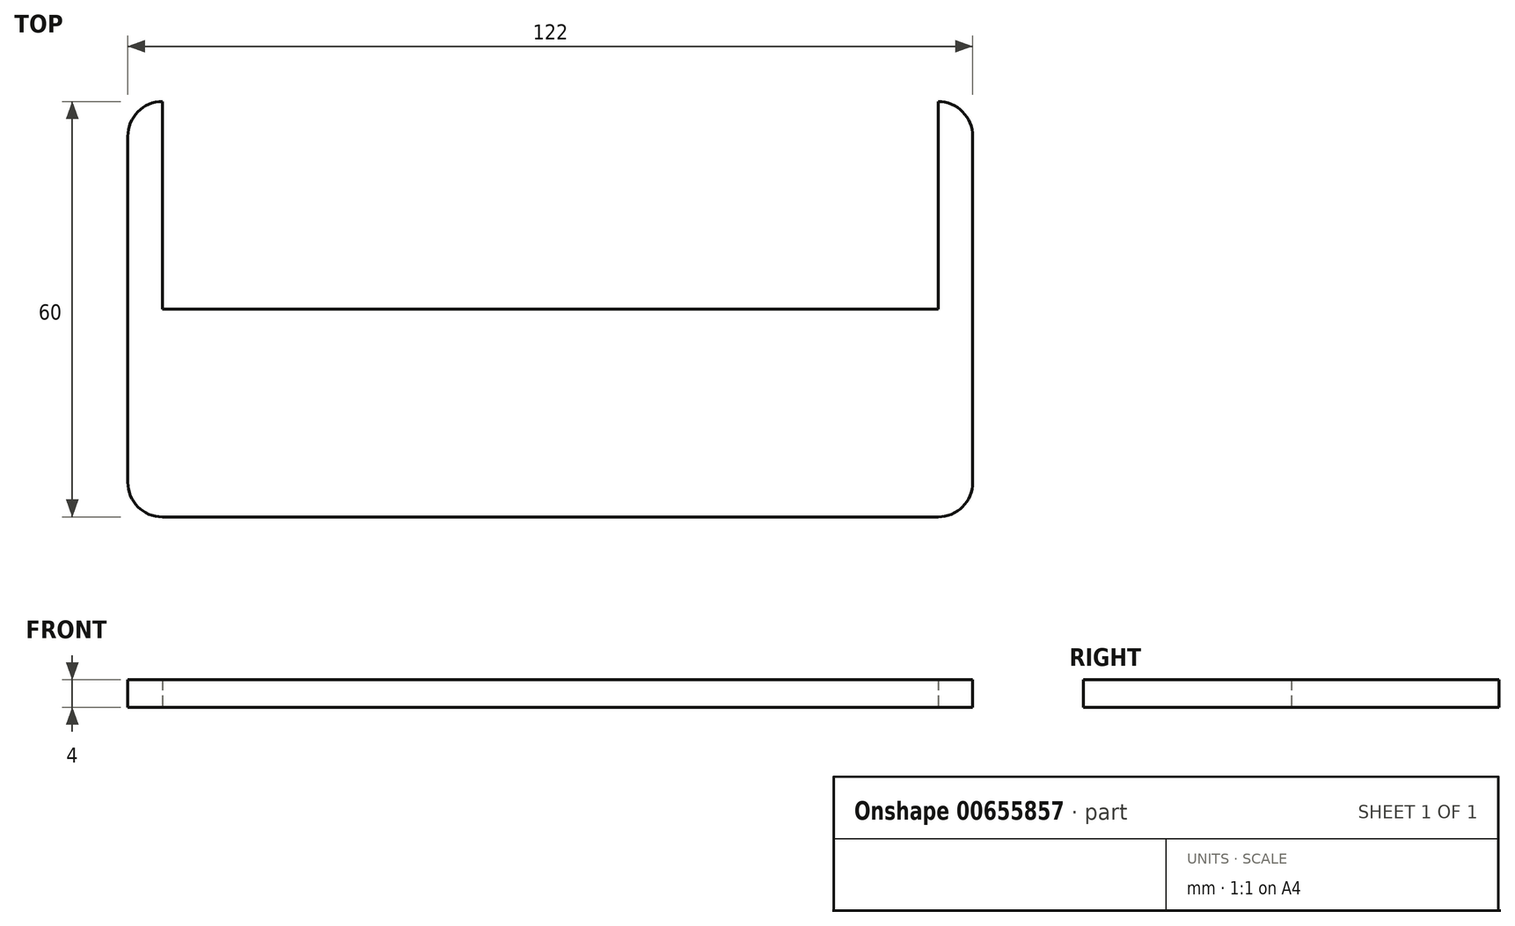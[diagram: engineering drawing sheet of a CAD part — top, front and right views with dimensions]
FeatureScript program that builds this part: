
annotation { "Feature Type Name" : "Feature", "Feature Type Description" : "" }
export const myFeature = defineFeature(function(context is Context, id is Id, definition is map)
    precondition{}
    {
        {
            var Q0;
            Q0=qCreatedBy(makeId("Top.planeOp"),FACE);
            var sketch = newSketch(context, id + "F0", { "sketchPlane" : qUnion([Q0])});
            skLineSegment(sketch, "E0.bottom", {"start": v(-56, 0) * mm, "end": v(56, 0) * mm});
            skLineSegment(sketch, "E0.top", {"start": v(-56, -30) * mm, "end": v(56, -30) * mm});
            skLineSegment(sketch, "E0.left", {"start": v(-56, 0) * mm, "end": v(-56, -30) * mm});
            skLineSegment(sketch, "E0.right", {"start": v(56, 0) * mm, "end": v(56, -30) * mm});
            skLineSegment(sketch, "E1.bottom", {"start": v(-56, -30) * mm, "end": v(-61, -30) * mm});
            skLineSegment(sketch, "E1.top", {"start": v(-56, 30) * mm, "end": v(-61, 30) * mm});
            skLineSegment(sketch, "E1.left", {"start": v(-56, -30) * mm, "end": v(-56, 30) * mm});
            skLineSegment(sketch, "E1.right", {"start": v(-61, -30) * mm, "end": v(-61, 30) * mm});
            skLineSegment(sketch, "E2.bottom", {"start": v(56, -30) * mm, "end": v(61, -30) * mm});
            skLineSegment(sketch, "E2.top", {"start": v(56, 30) * mm, "end": v(61, 30) * mm});
            skLineSegment(sketch, "E2.left", {"start": v(56, -30) * mm, "end": v(56, 30) * mm});
            skLineSegment(sketch, "E2.right", {"start": v(61, -30) * mm, "end": v(61, 30) * mm});
            skSolve(sketch);
        }
        {
            var Q0;
            Q0 = qSketchRegion(id + "F0", true);
            extrude(context, id + "F1", {"entities" : qUnion([Q0]), "depth" : 4 * mm, "offsetDistance" : 25 * mm});
        }
        {
            var Q0;
            Q0=makeQuery(id+"F1.opExtrude","SWEPT_EDGE",EDGE,{"disambiguationData":[OSD([sQuery(id+"F0.wireOp",EDGE,"E1.bottom"),sQuery(id+"F0.wireOp",EDGE,"E1.right")])]});
            var Q1;
            Q1=makeQuery(id+"F1.opExtrude","SWEPT_EDGE",EDGE,{"disambiguationData":[OSD([sQuery(id+"F0.wireOp",EDGE,"E2.bottom"),sQuery(id+"F0.wireOp",EDGE,"E2.right")])]});
            var Q2;
            Q2=makeQuery(id+"F1.opExtrude","SWEPT_EDGE",EDGE,{"disambiguationData":[OSD([sQuery(id+"F0.wireOp",EDGE,"E2.top"),sQuery(id+"F0.wireOp",EDGE,"E2.right")])]});
            var Q3;
            Q3=makeQuery(id+"F1.opExtrude","SWEPT_EDGE",EDGE,{"disambiguationData":[OSD([sQuery(id+"F0.wireOp",EDGE,"E1.top"),sQuery(id+"F0.wireOp",EDGE,"E1.right")])]});
            fillet(context, id + "F2", {"entities" : qUnion([Q0, Q1, Q2, Q3]), "radius" : 5 * mm, "tangentPropagation" : true, "allowEdgeOverflow" : false});
        }
    });
